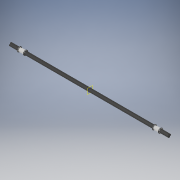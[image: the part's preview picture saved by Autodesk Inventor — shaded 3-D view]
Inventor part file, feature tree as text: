
AUTODESK INVENTOR PART (.ipt)
format: ipt  version: 2019 (Build 230136000, 136)  size: 279,040 bytes
history: native  units: in
note: dims shown in document units (in); Inventor stores cm internally (conversion verified against a paired STEP export)
features: extrude x6, sketch x6, plane x5, mirror x3, fillet x2
ambient origin geometry x8: Origin, YZ Plane, XZ Plane, XY Plane, X Axis, Y Axis, Z Axis, Center Point
bodies: Solid1 (feature_tree)
feature tree (22):
  extrude  "Extrusion1"  Depth=0.0689in
  fillet  "Fillet1"  Radius=0.0689in
  extrude  "Extrusion2"  Depth=0.1772in
  plane  "Work Plane1"
  mirror  "Mirror1"
  plane  "Work Plane2"
  extrude  "Extrusion3"  Depth=0.1095in
  plane  "Work Plane3"
  extrude  "Extrusion4"  Depth=0.1093in
  extrude  "Extrusion5"  Depth=8.0464in TaperAngle=0.0deg
  extrude  "Extrusion6"  Depth=0.0118in
  plane  "Work Plane4"
  mirror  "Mirror2"
  fillet  "Fillet2"  Radius=0.0059in
  plane  "Work Plane5"
  mirror  "Mirror3"
  sketch  "Sketch1"  dims[d3=0.0689in d4=0.0689in d5=0.0886in d10=0.1721in d12=0.0702in d13=0.0703in d14=0.0673in d15=0.1881in d16=0.5231in d17=0.0886in d18=0.0689in d19=0.0689in]
  sketch  "Sketch2"  dims[d20=0.1772in d21=0.1098in]
  sketch  "Sketch3"  dims[d22=0.0676in d23=0.1095in]
  sketch  "Sketch4"  dims[d24=0.1018in d25=0.1093in]
  sketch  "Sketch5"  dims[d26=0.1093in d27=8.0464in d28=0.0in]
  sketch  "Sketch6"  dims[d29=0.0118in d30=0.0591in d31=0.0059in d32=0.0in d33=-0.4375in d34=0.0866in d35=0.2362in d36=0.0312in d37=0.0in d38=0.0in d39=0.0866in d40=0.2812in d41=0.0in d42=0.2362in d43=0.0866in d44=0.0312in d45=0.0in d46=0.0039in d47=0.0in d48=0.0118in]
